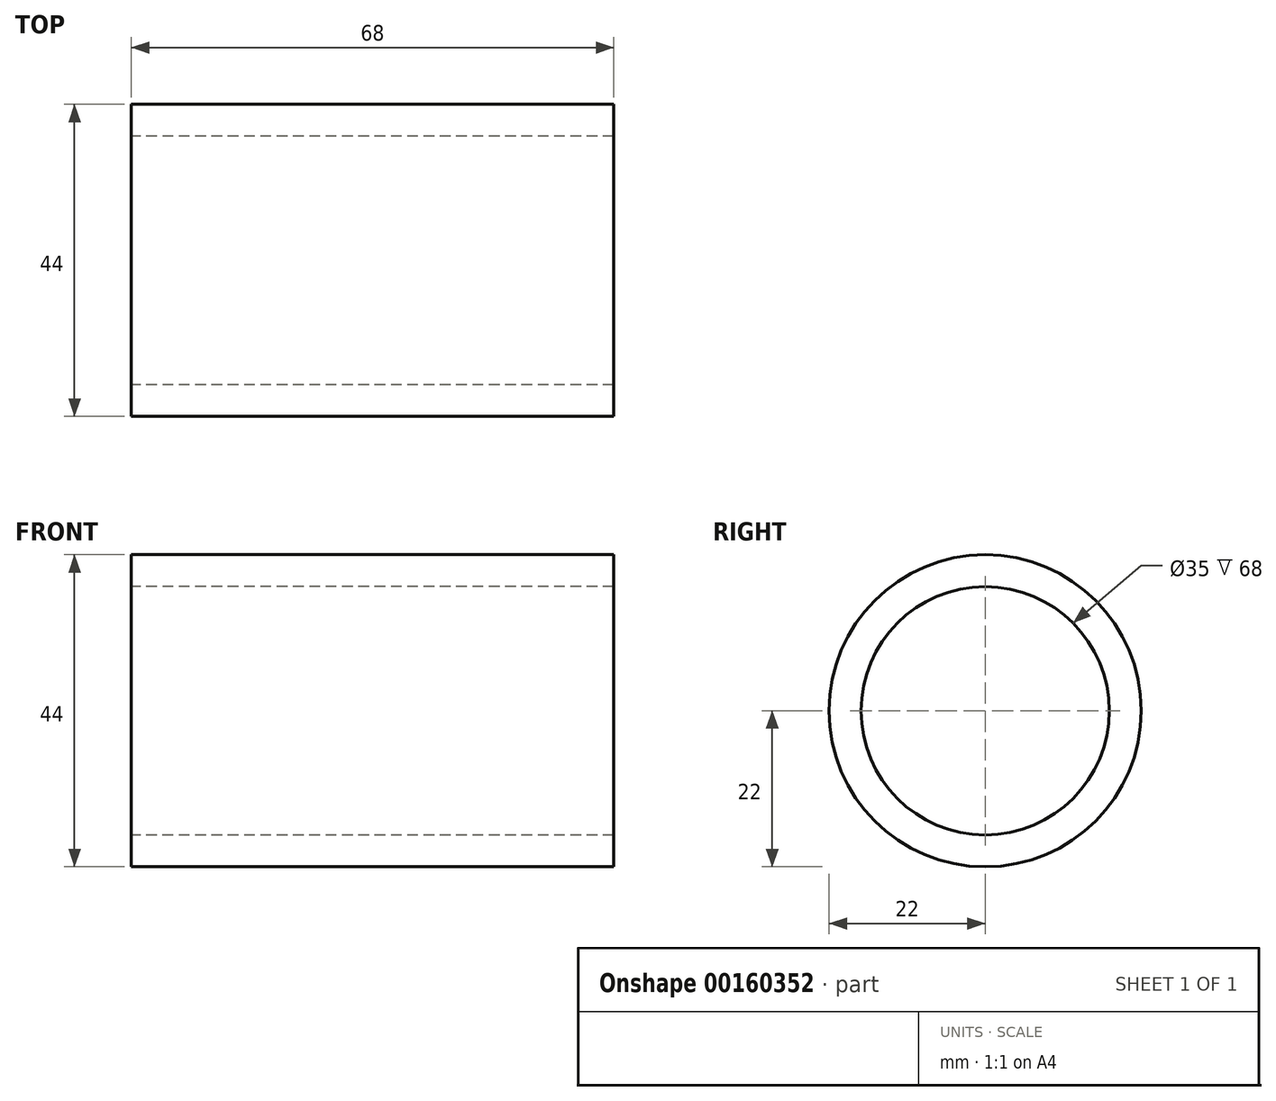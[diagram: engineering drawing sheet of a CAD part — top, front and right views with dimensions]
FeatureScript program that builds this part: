
annotation { "Feature Type Name" : "Feature", "Feature Type Description" : "" }
export const myFeature = defineFeature(function(context is Context, id is Id, definition is map)
    precondition{}
    {
        {
            assignVariable(context, id + "F0", {"name" : "BBwidth", "anyValue" : 68});
        }
        {
            var Q0;
            Q0=qCreatedBy(makeId("Right.planeOp"),FACE);
            var sketch = newSketch(context, id + "F1", { "sketchPlane" : qUnion([Q0])});
            skCircle(sketch, "E0", {"center": v(0, 0) * mm, "radius": 17.5 * mm});
            skCircle(sketch, "E1", {"center": v(0, 0) * mm, "radius": 22 * mm});
            skLineSegment(sketch, "E2", {"start": v(0, 0) * mm, "end": v(-121.83, 359.94) * mm});
            skCircle(sketch, "E3", {"center": v(-419.51, 20.2) * mm, "radius": 330.2 * mm});
            skCircle(sketch, "E4", {"center": v(641.32, 20.2) * mm, "radius": 330.2 * mm});
            skLineSegment(sketch, "E5", {"start": v(-121.83, 359.94) * mm, "end": v(-182.1, 537.97) * mm, "construction": true});
            skLineSegment(sketch, "E6", {"start": v(-182.1, 537.97) * mm, "end": v(387.9, 537.97) * mm, "construction": true});
            skLineSegment(sketch, "E7", {"start": v(603.3, 4.84) * mm, "end": v(425.37, 445.25) * mm, "construction": true});
            skLineSegment(sketch, "E8", {"start": v(603.3, 4.84) * mm, "end": v(641.32, 20.2) * mm, "construction": true});
            skLineSegment(sketch, "E9", {"start": v(425.37, 445.25) * mm, "end": v(387.9, 537.97) * mm});
            skLineSegment(sketch, "E10", {"start": v(425.37, 445.25) * mm, "end": v(463.38, 460.61) * mm, "construction": true});
            skLineSegment(sketch, "E11", {"start": v(-419.51, -310) * mm, "end": v(641.32, -310) * mm, "construction": true});
            skLineSegment(sketch, "E12", {"start": v(387.9, 537.97) * mm, "end": v(-112.21, 331.52) * mm});
            skLineSegment(sketch, "E13", {"start": v(463.38, 460.61) * mm, "end": v(641.32, 20.2) * mm, "construction": true});
            skCircle(sketch, "E14", {"center": v(596.37, 131.46) * mm, "radius": 330.2 * mm, "construction": true});
            skLineSegment(sketch, "E15", {"start": v(425.37, 445.25) * mm, "end": v(16.44, -14.62) * mm});
            skSolve(sketch);
        }
        {
            var Q0;
            Q0=makeQuery(id+"F1.imprint","IMPRINT",FACE,{"disambiguationData":[TD([[makeQuery(id+"F1.imprint","IMPRINT",EDGE,{"derivedFrom":sQuery(id+"F1.wireOp",EDGE,"E0")}),-1.0]])]});
            extrude(context, id + "F2", {"entities" : qUnion([Q0]), "depth" : (getVariable(context, 'BBwidth') / 2) * mm, "hasSecondDirection" : true, "secondDirectionOppositeDirection" : true, "secondDirectionDepth" : (getVariable(context, 'BBwidth') / 2) * mm});
        }
    });
